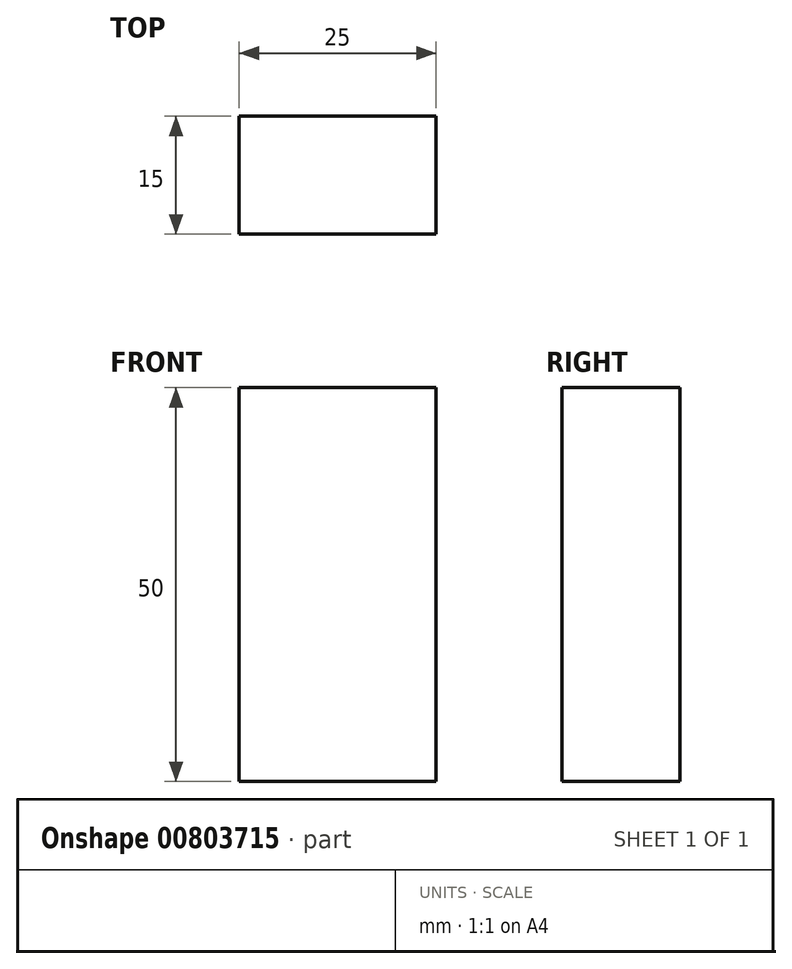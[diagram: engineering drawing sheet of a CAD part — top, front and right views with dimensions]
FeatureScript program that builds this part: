
annotation { "Feature Type Name" : "Feature", "Feature Type Description" : "" }
export const myFeature = defineFeature(function(context is Context, id is Id, definition is map)
    precondition{}
    {
        {
            var Q0;
            Q0=qCreatedBy(makeId("Top.planeOp"),FACE);
            var sketch = newSketch(context, id + "F0", { "sketchPlane" : qUnion([Q0])});
            skLineSegment(sketch, "E0.bottom", {"start": v(-45.47, 40.86) * mm, "end": v(-20.47, 40.86) * mm});
            skLineSegment(sketch, "E0.top", {"start": v(-45.47, 25.86) * mm, "end": v(-20.47, 25.86) * mm});
            skLineSegment(sketch, "E0.left", {"start": v(-45.47, 40.86) * mm, "end": v(-45.47, 25.86) * mm});
            skLineSegment(sketch, "E0.right", {"start": v(-20.47, 40.86) * mm, "end": v(-20.47, 25.86) * mm});
            skSolve(sketch);
        }
        {
            var Q0;
            Q0 = qSketchRegion(id + "F0", true);
            extrude(context, id + "F1", {"entities" : qUnion([Q0]), "depth" : 50 * mm, "offsetDistance" : 25 * mm});
        }
    });
